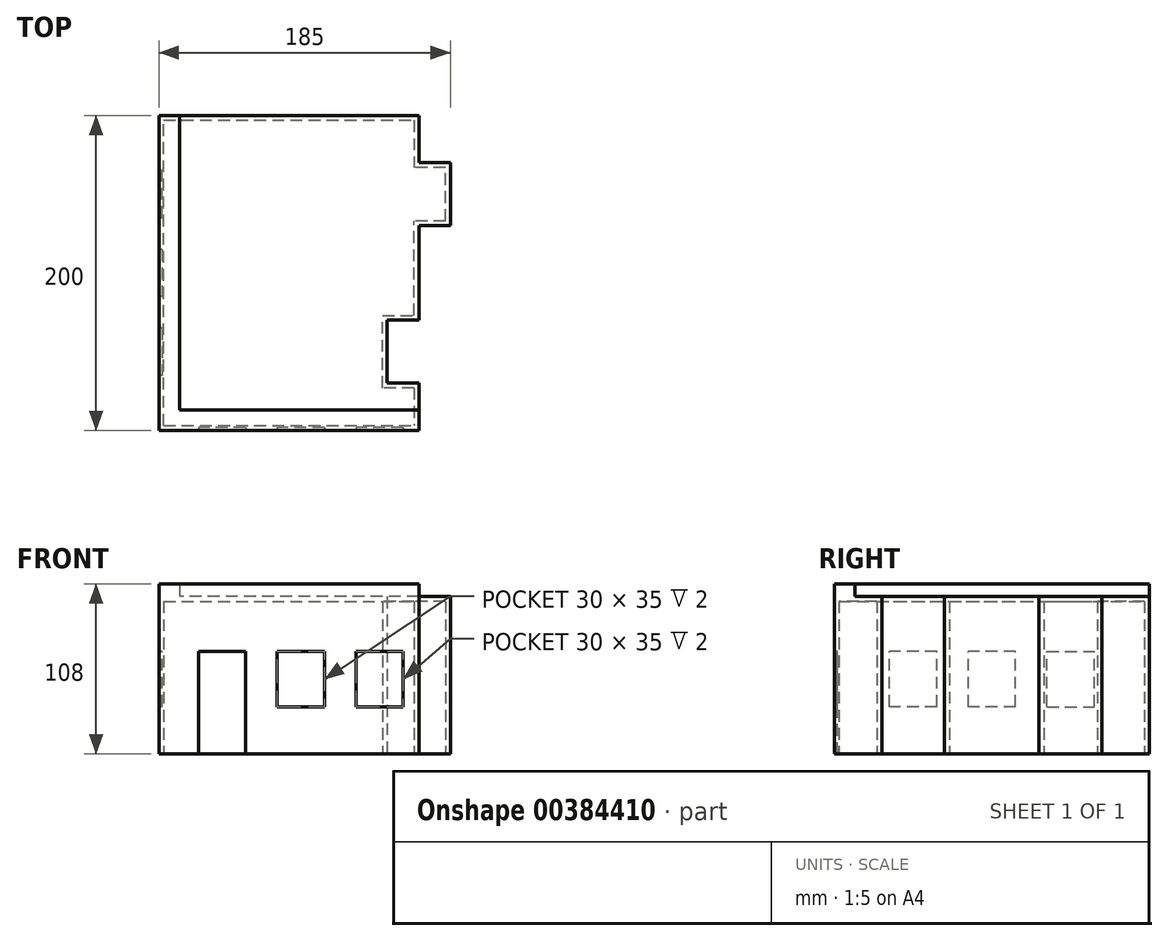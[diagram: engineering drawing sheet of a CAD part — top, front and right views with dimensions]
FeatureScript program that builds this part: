
annotation { "Feature Type Name" : "Feature", "Feature Type Description" : "" }
export const myFeature = defineFeature(function(context is Context, id is Id, definition is map)
    precondition{}
    {
        {
            var Q0;
            Q0=qCreatedBy(makeId("Top.planeOp"),FACE);
            var sketch = newSketch(context, id + "F0", { "sketchPlane" : qUnion([Q0])});
            skLineSegment(sketch, "E0.bottom", {"start": v(0, -100) * mm, "end": v(-165, -100) * mm});
            skLineSegment(sketch, "E0.top", {"start": v(0, 100) * mm, "end": v(-165, 100) * mm});
            skLineSegment(sketch, "E0.right", {"start": v(-165, -100) * mm, "end": v(-165, 100) * mm});
            skPoint(sketch, "E0.middle", {"position": v(0, 0) * mm});
            skLineSegment(sketch, "E1", {"start": v(0, 100) * mm, "end": v(0, 70) * mm});
            skLineSegment(sketch, "E2", {"start": v(0, -100) * mm, "end": v(0, -70) * mm});
            skLineSegment(sketch, "E3.bottom", {"start": v(20, 30) * mm, "end": v(0, 30) * mm});
            skLineSegment(sketch, "E3.top", {"start": v(20, 70) * mm, "end": v(0, 70) * mm});
            skLineSegment(sketch, "E3.left", {"start": v(20, 30) * mm, "end": v(20, 70) * mm});
            skPoint(sketch, "E3.middle", {"position": v(0, 50) * mm});
            skLineSegment(sketch, "E4.bottom", {"start": v(0, -70) * mm, "end": v(-20, -70) * mm});
            skLineSegment(sketch, "E4.top", {"start": v(0, -30) * mm, "end": v(-20, -30) * mm});
            skLineSegment(sketch, "E4.right", {"start": v(-20, -70) * mm, "end": v(-20, -30) * mm});
            skPoint(sketch, "E4.middle", {"position": v(0, -50) * mm});
            skPoint(sketch, "E5.orphan", {"position": v(-20, 70) * mm});
            skPoint(sketch, "E6.orphan", {"position": v(-20, 30) * mm});
            skPoint(sketch, "E7.orphan", {"position": v(20, -30) * mm});
            skPoint(sketch, "E8.orphan", {"position": v(20, -70) * mm});
            skLineSegment(sketch, "E9.trimOffspring", {"start": v(0, -70) * mm, "end": v(0, -100) * mm});
            skLineSegment(sketch, "E10", {"start": v(-165, -100) * mm, "end": v(0, -100) * mm});
            skLineSegment(sketch, "E11", {"start": v(-165, 100) * mm, "end": v(0, 100) * mm});
            skLineSegment(sketch, "E12", {"start": v(-20, -30) * mm, "end": v(0, -30) * mm});
            skLineSegment(sketch, "E13", {"start": v(0, 30) * mm, "end": v(20, 30) * mm});
            skLineSegment(sketch, "E14", {"start": v(0, 70) * mm, "end": v(20, 70) * mm});
            skLineSegment(sketch, "E15", {"start": v(20, 70) * mm, "end": v(20, 30) * mm});
            skLineSegment(sketch, "E16", {"start": v(0, -30) * mm, "end": v(0, 30) * mm});
            skPoint(sketch, "E0.left.start.orphan", {"position": v(165, -100) * mm});
            skPoint(sketch, "E17.orphan", {"position": v(165, 100) * mm});
            skLineSegment(sketch, "E18.0", {"start": v(-162, -97) * mm, "end": v(-162, 97) * mm});
            skLineSegment(sketch, "E18.1", {"start": v(-23, -27) * mm, "end": v(-3, -27) * mm});
            skLineSegment(sketch, "E18.2", {"start": v(-23, -73) * mm, "end": v(-23, -27) * mm});
            skLineSegment(sketch, "E18.3", {"start": v(-3, -73) * mm, "end": v(-23, -73) * mm});
            skLineSegment(sketch, "E18.4", {"start": v(-3, -73) * mm, "end": v(-3, -97) * mm});
            skLineSegment(sketch, "E18.5", {"start": v(-3, -27) * mm, "end": v(-3, 33) * mm});
            skLineSegment(sketch, "E18.6", {"start": v(-162, -97) * mm, "end": v(-3, -97) * mm});
            skLineSegment(sketch, "E18.7", {"start": v(17, 33) * mm, "end": v(-3, 33) * mm});
            skLineSegment(sketch, "E18.8", {"start": v(17, 33) * mm, "end": v(17, 67) * mm});
            skLineSegment(sketch, "E18.9", {"start": v(17, 67) * mm, "end": v(-3, 67) * mm});
            skLineSegment(sketch, "E18.10", {"start": v(-3, 97) * mm, "end": v(-3, 67) * mm});
            skLineSegment(sketch, "E18.11", {"start": v(-162, 97) * mm, "end": v(-3, 97) * mm});
            skSolve(sketch);
        }
        {
            var Q0;
            Q0=makeQuery(id+"F0.imprint","IMPRINT",FACE,{"disambiguationData":[TD([[makeQuery(id+"F0.imprint","IMPRINT",EDGE,{"derivedFrom":sQuery(id+"F0.wireOp",EDGE,"E4.right")}),1.0]])]});
            extrude(context, id + "F1", {"entities" : qUnion([Q0]), "depth" : 100 * mm});
        }
        {
            var Q0;
            Q0=makeQuery(id+"F1.opExtrude","CAP_FACE",FACE,{"disambiguationData":[OSD([sQuery(id+"F0.wireOp",EDGE,"E4.right"),sQuery(id+"F0.wireOp",EDGE,"E9.trimOffspring"),sQuery(id+"F0.wireOp",EDGE,"E4.bottom"),sQuery(id+"F0.wireOp",EDGE,"E12"),sQuery(id+"F0.wireOp",EDGE,"E0.right"),sQuery(id+"F0.wireOp",EDGE,"E11"),sQuery(id+"F0.wireOp",EDGE,"E1"),sQuery(id+"F0.wireOp",EDGE,"E14"),sQuery(id+"F0.wireOp",EDGE,"E15"),sQuery(id+"F0.wireOp",EDGE,"E3.bottom"),sQuery(id+"F0.wireOp",EDGE,"E16"),sQuery(id+"F0.wireOp",EDGE,"E10"),sQuery(id+"F0.wireOp",EDGE,"e3cef52f-6f7f-4157-a51c-63866692d245.0"),sQuery(id+"F0.wireOp",EDGE,"e3cef52f-6f7f-4157-a51c-63866692d245.1"),sQuery(id+"F0.wireOp",EDGE,"e3cef52f-6f7f-4157-a51c-63866692d245.2"),sQuery(id+"F0.wireOp",EDGE,"e3cef52f-6f7f-4157-a51c-63866692d245.3"),sQuery(id+"F0.wireOp",EDGE,"e3cef52f-6f7f-4157-a51c-63866692d245.4"),sQuery(id+"F0.wireOp",EDGE,"e3cef52f-6f7f-4157-a51c-63866692d245.5"),sQuery(id+"F0.wireOp",EDGE,"e3cef52f-6f7f-4157-a51c-63866692d245.6"),sQuery(id+"F0.wireOp",EDGE,"e3cef52f-6f7f-4157-a51c-63866692d245.7"),sQuery(id+"F0.wireOp",EDGE,"e3cef52f-6f7f-4157-a51c-63866692d245.8"),sQuery(id+"F0.wireOp",EDGE,"e3cef52f-6f7f-4157-a51c-63866692d245.9"),sQuery(id+"F0.wireOp",EDGE,"e3cef52f-6f7f-4157-a51c-63866692d245.10"),sQuery(id+"F0.wireOp",EDGE,"e3cef52f-6f7f-4157-a51c-63866692d245.11")])],"isStart":false});
            var sketch = newSketch(context, id + "F2", { "sketchPlane" : qUnion([Q0])});
            skLineSegment(sketch, "E19", {"start": v(-165, -100) * mm, "end": v(0, -100) * mm});
            skLineSegment(sketch, "E20", {"start": v(0, -100) * mm, "end": v(0, -70) * mm});
            skLineSegment(sketch, "E21", {"start": v(0, -70) * mm, "end": v(-20, -70) * mm});
            skLineSegment(sketch, "E22", {"start": v(-20, -70) * mm, "end": v(-20, -30) * mm});
            skLineSegment(sketch, "E23", {"start": v(-20, -30) * mm, "end": v(0, -30) * mm});
            skLineSegment(sketch, "E24", {"start": v(0, -30) * mm, "end": v(0, 30) * mm});
            skLineSegment(sketch, "E25", {"start": v(0, 30) * mm, "end": v(20, 30) * mm});
            skLineSegment(sketch, "E26", {"start": v(20, 30) * mm, "end": v(20, 70) * mm});
            skLineSegment(sketch, "E27", {"start": v(20, 70) * mm, "end": v(0, 70) * mm});
            skLineSegment(sketch, "E28", {"start": v(0, 70) * mm, "end": v(0, 100) * mm});
            skLineSegment(sketch, "E29", {"start": v(0, 100) * mm, "end": v(-165, 100) * mm});
            skLineSegment(sketch, "E30", {"start": v(-165, 100) * mm, "end": v(-165, -100) * mm});
            skSolve(sketch);
        }
        {
            var Q0;
            Q0=qSketchRegion(id+"F2",true);
            extrude(context, id + "F3", {"entities" : qUnion([Q0]), "operationType" : NewBodyOperationType.ADD, "oppositeDirection" : true, "depth" : 3 * mm});
        }
        {
            var Q0;
            Q0=makeQuery(id+"F3.boolean.opBoolean","MERGE",FACE,{"derivedFrom":[makeQuery(id+"F1.opExtrude","CAP_FACE",FACE,{"disambiguationData":[OSD([sQuery(id+"F0.wireOp",EDGE,"E4.right"),sQuery(id+"F0.wireOp",EDGE,"E9.trimOffspring"),sQuery(id+"F0.wireOp",EDGE,"E4.bottom"),sQuery(id+"F0.wireOp",EDGE,"E12"),sQuery(id+"F0.wireOp",EDGE,"E0.right"),sQuery(id+"F0.wireOp",EDGE,"E11"),sQuery(id+"F0.wireOp",EDGE,"E1"),sQuery(id+"F0.wireOp",EDGE,"E14"),sQuery(id+"F0.wireOp",EDGE,"E15"),sQuery(id+"F0.wireOp",EDGE,"E3.bottom"),sQuery(id+"F0.wireOp",EDGE,"E16"),sQuery(id+"F0.wireOp",EDGE,"E10"),sQuery(id+"F0.wireOp",EDGE,"e3cef52f-6f7f-4157-a51c-63866692d245.0"),sQuery(id+"F0.wireOp",EDGE,"e3cef52f-6f7f-4157-a51c-63866692d245.1"),sQuery(id+"F0.wireOp",EDGE,"e3cef52f-6f7f-4157-a51c-63866692d245.2"),sQuery(id+"F0.wireOp",EDGE,"e3cef52f-6f7f-4157-a51c-63866692d245.3"),sQuery(id+"F0.wireOp",EDGE,"e3cef52f-6f7f-4157-a51c-63866692d245.4"),sQuery(id+"F0.wireOp",EDGE,"e3cef52f-6f7f-4157-a51c-63866692d245.5"),sQuery(id+"F0.wireOp",EDGE,"e3cef52f-6f7f-4157-a51c-63866692d245.6"),sQuery(id+"F0.wireOp",EDGE,"e3cef52f-6f7f-4157-a51c-63866692d245.7"),sQuery(id+"F0.wireOp",EDGE,"e3cef52f-6f7f-4157-a51c-63866692d245.8"),sQuery(id+"F0.wireOp",EDGE,"e3cef52f-6f7f-4157-a51c-63866692d245.9"),sQuery(id+"F0.wireOp",EDGE,"e3cef52f-6f7f-4157-a51c-63866692d245.10"),sQuery(id+"F0.wireOp",EDGE,"e3cef52f-6f7f-4157-a51c-63866692d245.11")])],"isStart":false}),makeQuery(id+"F3.opExtrude","CAP_FACE",FACE,{"disambiguationData":[OSD([sQuery(id+"F2.wireOp",EDGE,"E19"),sQuery(id+"F2.wireOp",EDGE,"E20"),sQuery(id+"F2.wireOp",EDGE,"E21"),sQuery(id+"F2.wireOp",EDGE,"E22"),sQuery(id+"F2.wireOp",EDGE,"E23"),sQuery(id+"F2.wireOp",EDGE,"E24"),sQuery(id+"F2.wireOp",EDGE,"E25"),sQuery(id+"F2.wireOp",EDGE,"E26"),sQuery(id+"F2.wireOp",EDGE,"E27"),sQuery(id+"F2.wireOp",EDGE,"E28"),sQuery(id+"F2.wireOp",EDGE,"E29"),sQuery(id+"F2.wireOp",EDGE,"E30")])],"isStart":true})]});
            var sketch = newSketch(context, id + "F4", { "sketchPlane" : qUnion([Q0])});
            skLineSegment(sketch, "E31.bottom", {"start": v(0, -100) * mm, "end": v(-162, -100) * mm});
            skLineSegment(sketch, "E31.top", {"start": v(0, -87) * mm, "end": v(-152, -87) * mm});
            skLineSegment(sketch, "E31.left", {"start": v(0, -100) * mm, "end": v(0, -87) * mm});
            skLineSegment(sketch, "E32.bottom", {"start": v(-165, -100) * mm, "end": v(-152, -100) * mm});
            skLineSegment(sketch, "E32.top", {"start": v(-165, 100) * mm, "end": v(-152, 100) * mm});
            skLineSegment(sketch, "E32.left", {"start": v(-165, -100) * mm, "end": v(-165, 100) * mm});
            skLineSegment(sketch, "E32.right", {"start": v(-152, -87) * mm, "end": v(-152, 100) * mm});
            skSolve(sketch);
        }
        {
            var Q0;
            Q0 = qSketchRegion(id + "F4", true);
            extrude(context, id + "F5", {"entities" : qUnion([Q0]), "operationType" : NewBodyOperationType.ADD, "depth" : 8 * mm});
        }
        {
            var Q0;
            Q0=makeQuery(id+"F5.boolean.opBoolean","MERGE",FACE,{"derivedFrom":[makeQuery(id+"F1.opExtrude","SWEPT_FACE",FACE,{"disambiguationData":[OSD([sQuery(id+"F0.wireOp",EDGE,"E10")])]}),makeQuery(id+"F5.opExtrude","SWEPT_FACE",FACE,{"disambiguationData":[OSD([sQuery(id+"F4.wireOp",EDGE,"E31.bottom"),sQuery(id+"F4.wireOp",EDGE,"E32.bottom")])]})]});
            var sketch = newSketch(context, id + "F6", { "sketchPlane" : qUnion([Q0])});
            skLineSegment(sketch, "E33.bottom", {"start": v(0, 0) * mm, "end": v(-10, 0) * mm, "construction": true});
            skLineSegment(sketch, "E33.top", {"start": v(0, 49.53) * mm, "end": v(-10, 49.53) * mm, "construction": true});
            skLineSegment(sketch, "E33.left", {"start": v(0, 0) * mm, "end": v(0, 49.53) * mm, "construction": true});
            skLineSegment(sketch, "E33.right", {"start": v(-10, 0) * mm, "end": v(-10, 49.53) * mm, "construction": true});
            skLineSegment(sketch, "E34.bottom", {"start": v(0, 0) * mm, "end": v(-165, 0) * mm, "construction": true});
            skLineSegment(sketch, "E34.top", {"start": v(0, 30) * mm, "end": v(-110, 30) * mm, "construction": true});
            skLineSegment(sketch, "E34.left", {"start": v(0, 0) * mm, "end": v(0, 30) * mm, "construction": true});
            skLineSegment(sketch, "E34.right", {"start": v(-165, 0) * mm, "end": v(-165, 30) * mm, "construction": true});
            skLineSegment(sketch, "E35.bottom", {"start": v(-10, 30) * mm, "end": v(-40, 30) * mm});
            skLineSegment(sketch, "E35.top", {"start": v(-10, 65) * mm, "end": v(-40, 65) * mm});
            skLineSegment(sketch, "E35.left", {"start": v(-10, 30) * mm, "end": v(-10, 65) * mm});
            skLineSegment(sketch, "E35.right", {"start": v(-40, 30) * mm, "end": v(-40, 65) * mm});
            skPoint(sketch, "E36.oppositeSnap0", {"position": v(-40, 47.5) * mm});
            skLineSegment(sketch, "E36.bottom", {"start": v(-40, 30) * mm, "end": v(-60, 30) * mm, "construction": true});
            skLineSegment(sketch, "E36.top", {"start": v(-40, 47.5) * mm, "end": v(-60, 47.5) * mm, "construction": true});
            skLineSegment(sketch, "E36.left", {"start": v(-40, 30) * mm, "end": v(-40, 47.5) * mm, "construction": true});
            skLineSegment(sketch, "E36.right", {"start": v(-60, 30) * mm, "end": v(-60, 47.5) * mm, "construction": true});
            skLineSegment(sketch, "E37.bottom", {"start": v(-60, 30) * mm, "end": v(-90, 30) * mm});
            skLineSegment(sketch, "E37.top", {"start": v(-60, 65) * mm, "end": v(-90, 65) * mm});
            skLineSegment(sketch, "E37.left", {"start": v(-60, 30) * mm, "end": v(-60, 65) * mm});
            skLineSegment(sketch, "E37.right", {"start": v(-90, 30) * mm, "end": v(-90, 65) * mm});
            skPoint(sketch, "E38.oppositeSnap0", {"position": v(-90, 47.5) * mm});
            skLineSegment(sketch, "E38.bottom", {"start": v(-90, 30) * mm, "end": v(-110, 30) * mm, "construction": true});
            skLineSegment(sketch, "E38.left", {"start": v(-90, 30) * mm, "end": v(-90, 47.5) * mm, "construction": true});
            skLineSegment(sketch, "E38.right", {"start": v(-110, 30) * mm, "end": v(-110, 47.5) * mm, "construction": true});
            skLineSegment(sketch, "E39.top", {"start": v(-110, 65) * mm, "end": v(-140, 65) * mm});
            skLineSegment(sketch, "E39.left", {"start": v(-110, 30) * mm, "end": v(-110, 65) * mm});
            skLineSegment(sketch, "E39.right", {"start": v(-140, 30) * mm, "end": v(-140, 65) * mm});
            skLineSegment(sketch, "E40.top", {"start": v(-140, 0) * mm, "end": v(-110, 0) * mm});
            skLineSegment(sketch, "E40.left", {"start": v(-140, 30) * mm, "end": v(-140, 0) * mm});
            skLineSegment(sketch, "E40.right", {"start": v(-110, 30) * mm, "end": v(-110, 0) * mm});
            skLineSegment(sketch, "E41.trimOffspring", {"start": v(-140, 30) * mm, "end": v(-165, 30) * mm, "construction": true});
            skSolve(sketch);
        }
        {
            var Q0;
            Q0 = qSketchRegion(id + "F6", true);
            extrude(context, id + "F7", {"entities" : qUnion([Q0]), "operationType" : NewBodyOperationType.REMOVE, "oppositeDirection" : true, "depth" : 2 * mm});
        }
        {
            var Q0;
            Q0=makeQuery(id+"F5.boolean.opBoolean","MERGE",FACE,{"derivedFrom":[makeQuery(id+"F1.opExtrude","SWEPT_FACE",FACE,{"disambiguationData":[OSD([sQuery(id+"F0.wireOp",EDGE,"E0.right")])]}),makeQuery(id+"F5.opExtrude","SWEPT_FACE",FACE,{"disambiguationData":[OSD([sQuery(id+"F4.wireOp",EDGE,"E32.left")])]})]});
            var sketch = newSketch(context, id + "F8", { "sketchPlane" : qUnion([Q0])});
            skLineSegment(sketch, "E42.bottom", {"start": v(-100, 0) * mm, "end": v(0, 0) * mm, "construction": true});
            skLineSegment(sketch, "E42.top", {"start": v(-100, 108) * mm, "end": v(0, 108) * mm, "construction": true});
            skLineSegment(sketch, "E42.left", {"start": v(-100, 0) * mm, "end": v(-100, 108) * mm, "construction": true});
            skLineSegment(sketch, "E42.right", {"start": v(0, 0) * mm, "end": v(0, 108) * mm, "construction": true});
            skLineSegment(sketch, "E43.bottom", {"start": v(-100, 0) * mm, "end": v(100, 0) * mm, "construction": true});
            skLineSegment(sketch, "E43.top", {"start": v(-100, 30) * mm, "end": v(100, 30) * mm, "construction": true});
            skLineSegment(sketch, "E43.left", {"start": v(-100, 0) * mm, "end": v(-100, 30) * mm, "construction": true});
            skLineSegment(sketch, "E43.right", {"start": v(100, 0) * mm, "end": v(100, 30) * mm, "construction": true});
            skLineSegment(sketch, "E44", {"start": v(0, 30) * mm, "end": v(0, 54) * mm});
            skLineSegment(sketch, "E45.bottom", {"start": v(-15, 30) * mm, "end": v(15, 30) * mm});
            skLineSegment(sketch, "E45.left", {"start": v(-15, 30) * mm, "end": v(-15, 65) * mm});
            skLineSegment(sketch, "E45.right", {"start": v(15, 30) * mm, "end": v(15, 65) * mm});
            skPoint(sketch, "E45.middle", {"position": v(0, 54) * mm});
            skLineSegment(sketch, "E46.top", {"start": v(-15, 65) * mm, "end": v(15, 65) * mm});
            skPoint(sketch, "E47.orphan", {"position": v(-15, 78) * mm});
            skPoint(sketch, "E48.orphan", {"position": v(15, 78) * mm});
            skLineSegment(sketch, "E49.bottom", {"start": v(15, 30) * mm, "end": v(35, 30) * mm, "construction": true});
            skLineSegment(sketch, "E49.top", {"start": v(15, 50) * mm, "end": v(35, 50) * mm, "construction": true});
            skLineSegment(sketch, "E49.left", {"start": v(15, 30) * mm, "end": v(15, 50) * mm, "construction": true});
            skLineSegment(sketch, "E49.right", {"start": v(35, 30) * mm, "end": v(35, 50) * mm, "construction": true});
            skLineSegment(sketch, "E50.bottom", {"start": v(35, 30) * mm, "end": v(65, 30) * mm});
            skLineSegment(sketch, "E50.top", {"start": v(35, 65) * mm, "end": v(65, 65) * mm});
            skLineSegment(sketch, "E50.left", {"start": v(35, 30) * mm, "end": v(35, 65) * mm});
            skLineSegment(sketch, "E50.right", {"start": v(65, 30) * mm, "end": v(65, 65) * mm});
            skLineSegment(sketch, "E51.bottom", {"start": v(-15, 30) * mm, "end": v(-35, 30) * mm, "construction": true});
            skLineSegment(sketch, "E51.top", {"start": v(-15, 52.54) * mm, "end": v(-35, 52.54) * mm, "construction": true});
            skLineSegment(sketch, "E51.left", {"start": v(-15, 30) * mm, "end": v(-15, 52.54) * mm, "construction": true});
            skLineSegment(sketch, "E51.right", {"start": v(-35, 30) * mm, "end": v(-35, 52.54) * mm, "construction": true});
            skLineSegment(sketch, "E52.bottom", {"start": v(-35, 30) * mm, "end": v(-65, 30) * mm});
            skLineSegment(sketch, "E52.top", {"start": v(-35, 65) * mm, "end": v(-65, 65) * mm});
            skLineSegment(sketch, "E52.left", {"start": v(-35, 30) * mm, "end": v(-35, 65) * mm});
            skLineSegment(sketch, "E52.right", {"start": v(-65, 30) * mm, "end": v(-65, 65) * mm});
            skSolve(sketch);
        }
        {
            var Q0;
            Q0 = qSketchRegion(id + "F8", true);
            extrude(context, id + "F9", {"entities" : qUnion([Q0]), "operationType" : NewBodyOperationType.REMOVE, "oppositeDirection" : true, "depth" : 2 * mm});
        }
    });
